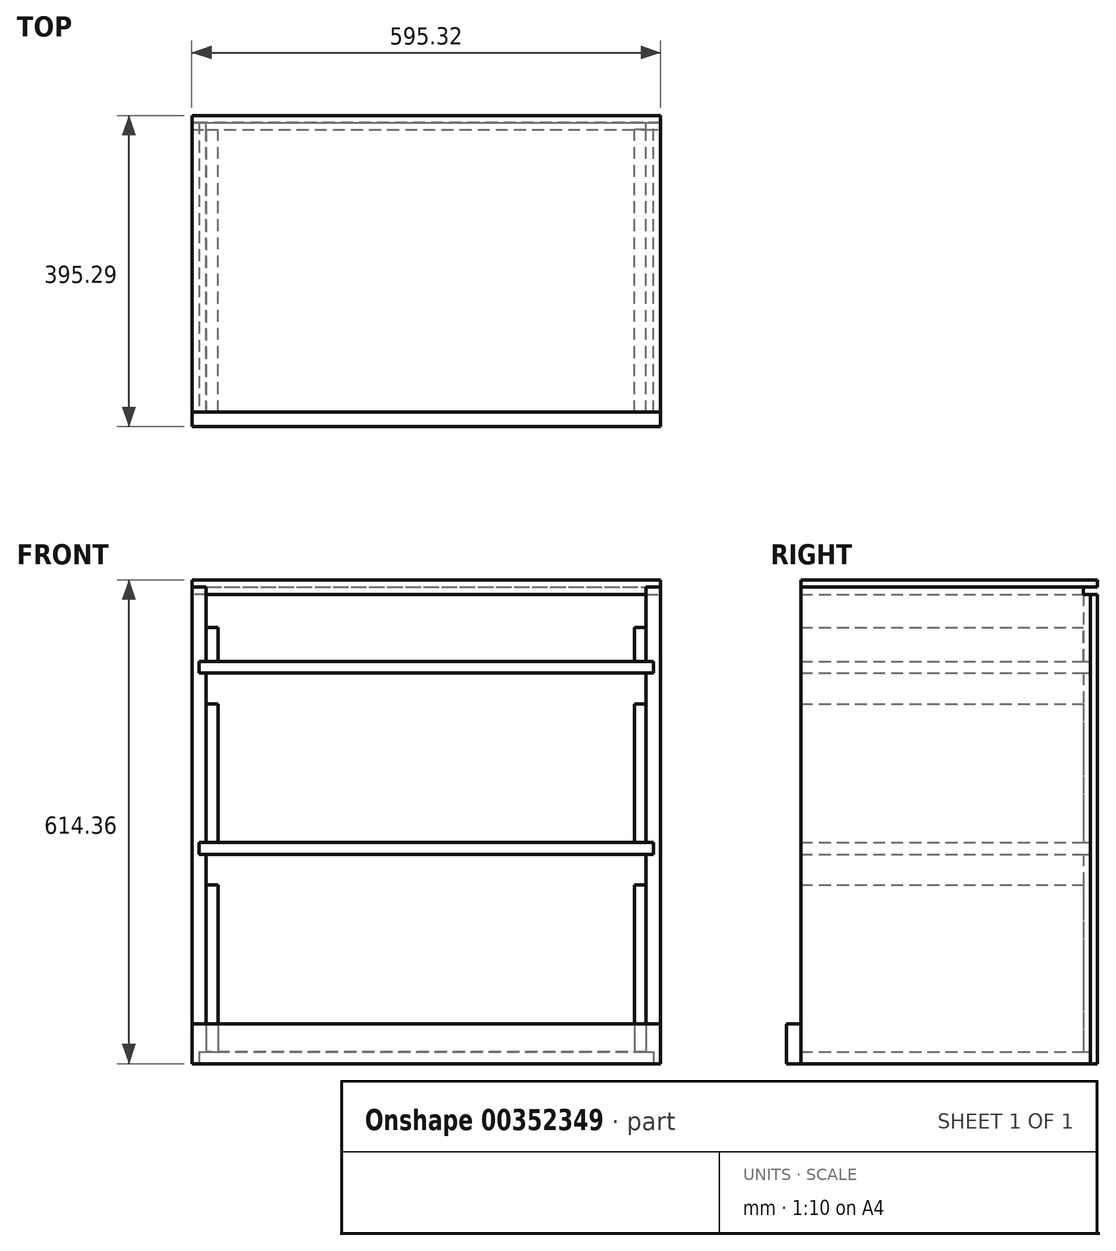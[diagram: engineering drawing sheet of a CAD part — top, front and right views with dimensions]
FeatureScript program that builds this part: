
annotation { "Feature Type Name" : "Feature", "Feature Type Description" : "" }
export const myFeature = defineFeature(function(context is Context, id is Id, definition is map)
    precondition{}
    {
        {
            var Q0;
            Q0=qCreatedBy(makeId("Top.planeOp"),FACE);
            var sketch = newSketch(context, id + "F0", { "sketchPlane" : qUnion([Q0])});
            skLineSegment(sketch, "E0.bottom", {"start": v(-266.7, 177.8) * mm, "end": v(266.7, 177.8) * mm, "construction": true});
            skLineSegment(sketch, "E0.top", {"start": v(-266.7, -177.8) * mm, "end": v(266.7, -177.8) * mm, "construction": true});
            skLineSegment(sketch, "E0.left", {"start": v(-266.7, 177.8) * mm, "end": v(-266.7, -177.8) * mm, "construction": true});
            skLineSegment(sketch, "E0.right", {"start": v(266.7, 177.8) * mm, "end": v(266.7, -177.8) * mm, "construction": true});
            skLineSegment(sketch, "E1", {"start": v(-297.66, 199.23) * mm, "end": v(-297.66, 190.1) * mm});
            skLineSegment(sketch, "E2", {"start": v(-297.66, 190.1) * mm, "end": v(-279.4, 190.1) * mm});
            skLineSegment(sketch, "E3", {"start": v(-279.4, 190.1) * mm, "end": v(-279.4, 180.97) * mm});
            skLineSegment(sketch, "E4.MirrorCS", {"start": v(279.4, 190.1) * mm, "end": v(279.4, 180.97) * mm});
            skLineSegment(sketch, "E5.MirrorCS", {"start": v(297.66, 199.23) * mm, "end": v(297.66, 190.1) * mm});
            skLineSegment(sketch, "E6.MirrorCS", {"start": v(297.66, 190.1) * mm, "end": v(279.4, 190.1) * mm});
            skLineSegment(sketch, "E7", {"start": v(-297.66, 199.23) * mm, "end": v(297.66, 199.23) * mm});
            skLineSegment(sketch, "E8", {"start": v(-279.4, 180.97) * mm, "end": v(279.4, 180.97) * mm});
            skLineSegment(sketch, "E9.bottom", {"start": v(-297.66, -196.06) * mm, "end": v(297.66, -196.06) * mm});
            skLineSegment(sketch, "E9.top", {"start": v(-297.66, -177.8) * mm, "end": v(297.66, -177.8) * mm});
            skLineSegment(sketch, "E9.left", {"start": v(-297.66, -196.06) * mm, "end": v(-297.66, -177.8) * mm});
            skLineSegment(sketch, "E9.right", {"start": v(297.66, -196.06) * mm, "end": v(297.66, -177.8) * mm});
            skSolve(sketch);
        }
        {
            var Q0;
            Q0=qCreatedBy(makeId("Top.planeOp"),FACE);
            var sketch = newSketch(context, id + "F1", { "sketchPlane" : qUnion([Q0])});
            skLineSegment(sketch, "E10.bottom", {"start": v(-297.66, 190.1) * mm, "end": v(-279.4, 190.1) * mm});
            skLineSegment(sketch, "E10.top", {"start": v(-297.66, -177.8) * mm, "end": v(-279.4, -177.8) * mm});
            skLineSegment(sketch, "E10.left", {"start": v(-297.66, 190.1) * mm, "end": v(-297.66, -177.8) * mm});
            skLineSegment(sketch, "E10.right", {"start": v(-279.4, 190.1) * mm, "end": v(-279.4, -177.8) * mm});
            skLineSegment(sketch, "E11.MirrorCS", {"start": v(297.66, -177.8) * mm, "end": v(279.4, -177.8) * mm});
            skLineSegment(sketch, "E12.MirrorCS", {"start": v(297.66, 190.1) * mm, "end": v(279.4, 190.1) * mm});
            skLineSegment(sketch, "E13.MirrorCS", {"start": v(297.66, 190.1) * mm, "end": v(297.66, -177.8) * mm});
            skLineSegment(sketch, "E14.MirrorCS", {"start": v(279.4, 190.1) * mm, "end": v(279.4, -177.8) * mm});
            skSolve(sketch);
        }
        {
            var Q0;
            Q0=qCreatedBy(makeId("Front.planeOp"),FACE);
            var sketch = newSketch(context, id + "F2", { "sketchPlane" : qUnion([Q0])});
            skLineSegment(sketch, "E15.bottom", {"start": v(-288.53, 15.08) * mm, "end": v(288.53, 15.08) * mm});
            skLineSegment(sketch, "E15.top", {"start": v(-288.53, 0) * mm, "end": v(288.53, 0) * mm});
            skLineSegment(sketch, "E15.left", {"start": v(-288.53, 15.08) * mm, "end": v(-288.53, 0) * mm});
            skLineSegment(sketch, "E15.right", {"start": v(288.53, 15.08) * mm, "end": v(288.53, 0) * mm});
            skLineSegment(sketch, "E16.bottom", {"start": v(-288.53, 280.99) * mm, "end": v(288.53, 280.99) * mm});
            skLineSegment(sketch, "E16.top", {"start": v(-288.53, 265.9) * mm, "end": v(288.53, 265.9) * mm});
            skLineSegment(sketch, "E16.left", {"start": v(-288.53, 280.99) * mm, "end": v(-288.53, 265.9) * mm});
            skLineSegment(sketch, "E16.right", {"start": v(288.53, 280.99) * mm, "end": v(288.53, 265.9) * mm});
            skLineSegment(sketch, "E17.bottom", {"start": v(-288.53, 511.18) * mm, "end": v(288.53, 511.18) * mm});
            skLineSegment(sketch, "E17.top", {"start": v(-288.53, 496.1) * mm, "end": v(288.53, 496.1) * mm});
            skLineSegment(sketch, "E17.left", {"start": v(-288.53, 511.18) * mm, "end": v(-288.53, 496.1) * mm});
            skLineSegment(sketch, "E17.right", {"start": v(288.53, 511.18) * mm, "end": v(288.53, 496.1) * mm});
            skLineSegment(sketch, "E18", {"start": v(-288.53, 605.23) * mm, "end": v(288.53, 605.23) * mm, "construction": true});
            skSolve(sketch);
        }
        {
            var Q0;
            Q0=qCreatedBy(makeId("Front.planeOp"),FACE);
            var sketch = newSketch(context, id + "F3", { "sketchPlane" : qUnion([Q0])});
            skLineSegment(sketch, "E19", {"start": v(-297.66, 614.36) * mm, "end": v(-297.66, 605.23) * mm});
            skLineSegment(sketch, "E20", {"start": v(-297.66, 605.23) * mm, "end": v(-279.4, 605.23) * mm});
            skLineSegment(sketch, "E21", {"start": v(-279.4, 605.23) * mm, "end": v(-279.4, 596.1) * mm});
            skLineSegment(sketch, "E22.MirrorCS", {"start": v(279.4, 605.23) * mm, "end": v(279.4, 596.1) * mm});
            skLineSegment(sketch, "E23.MirrorCS", {"start": v(297.66, 605.23) * mm, "end": v(279.4, 605.23) * mm});
            skLineSegment(sketch, "E24.MirrorCS", {"start": v(297.66, 614.36) * mm, "end": v(297.66, 605.23) * mm});
            skLineSegment(sketch, "E25", {"start": v(-297.66, 614.36) * mm, "end": v(297.66, 614.36) * mm});
            skLineSegment(sketch, "E26", {"start": v(-279.4, 596.1) * mm, "end": v(279.4, 596.1) * mm});
            skSolve(sketch);
        }
        {
            var Q0;
            Q0=qCreatedBy(makeId("Front.planeOp"),FACE);
            var sketch = newSketch(context, id + "F4", { "sketchPlane" : qUnion([Q0])});
            skLineSegment(sketch, "E27.bottom", {"start": v(-279.4, 227.01) * mm, "end": v(-264.32, 227.01) * mm});
            skLineSegment(sketch, "E27.top", {"start": v(-279.4, 15.08) * mm, "end": v(-264.32, 15.08) * mm});
            skLineSegment(sketch, "E27.left", {"start": v(-279.4, 227.01) * mm, "end": v(-279.4, 15.08) * mm});
            skLineSegment(sketch, "E27.right", {"start": v(-264.32, 227.01) * mm, "end": v(-264.32, 15.08) * mm});
            skLineSegment(sketch, "E28.bottom", {"start": v(-279.4, 457.2) * mm, "end": v(-264.32, 457.2) * mm});
            skLineSegment(sketch, "E28.top", {"start": v(-279.4, 280.99) * mm, "end": v(-264.32, 280.99) * mm});
            skLineSegment(sketch, "E28.left", {"start": v(-279.4, 457.2) * mm, "end": v(-279.4, 280.99) * mm});
            skLineSegment(sketch, "E28.right", {"start": v(-264.32, 457.2) * mm, "end": v(-264.32, 280.99) * mm});
            skLineSegment(sketch, "E29.bottom", {"start": v(-279.4, 511.18) * mm, "end": v(-264.32, 511.18) * mm});
            skLineSegment(sketch, "E29.top", {"start": v(-279.4, 554.04) * mm, "end": v(-264.32, 554.04) * mm});
            skLineSegment(sketch, "E29.left", {"start": v(-279.4, 511.18) * mm, "end": v(-279.4, 554.04) * mm});
            skLineSegment(sketch, "E29.right", {"start": v(-264.32, 511.18) * mm, "end": v(-264.32, 554.04) * mm});
            skLineSegment(sketch, "E30.MirrorCS", {"start": v(279.4, 280.99) * mm, "end": v(264.32, 280.99) * mm});
            skLineSegment(sketch, "E31.MirrorCS", {"start": v(279.4, 457.2) * mm, "end": v(264.32, 457.2) * mm});
            skLineSegment(sketch, "E32.MirrorCS", {"start": v(279.4, 15.08) * mm, "end": v(264.32, 15.08) * mm});
            skLineSegment(sketch, "E33.MirrorCS", {"start": v(279.4, 554.04) * mm, "end": v(264.32, 554.04) * mm});
            skLineSegment(sketch, "E34.MirrorCS", {"start": v(279.4, 511.18) * mm, "end": v(264.32, 511.18) * mm});
            skLineSegment(sketch, "E35.MirrorCS", {"start": v(279.4, 227.01) * mm, "end": v(264.32, 227.01) * mm});
            skLineSegment(sketch, "E36.MirrorCS", {"start": v(264.32, 227.01) * mm, "end": v(264.32, 15.08) * mm});
            skLineSegment(sketch, "E37.MirrorCS", {"start": v(279.4, 227.01) * mm, "end": v(279.4, 15.08) * mm});
            skLineSegment(sketch, "E38.MirrorCS", {"start": v(264.32, 511.18) * mm, "end": v(264.32, 554.04) * mm});
            skLineSegment(sketch, "E39.MirrorCS", {"start": v(279.4, 511.18) * mm, "end": v(279.4, 554.04) * mm});
            skLineSegment(sketch, "E40.MirrorCS", {"start": v(264.32, 457.2) * mm, "end": v(264.32, 280.99) * mm});
            skLineSegment(sketch, "E41.MirrorCS", {"start": v(279.4, 457.2) * mm, "end": v(279.4, 280.99) * mm});
            skLineSegment(sketch, "E42", {"start": v(-279.4, 457.2) * mm, "end": v(-279.4, 496.1) * mm, "construction": true});
            skLineSegment(sketch, "E43", {"start": v(-279.4, 227.01) * mm, "end": v(-279.4, 265.9) * mm, "construction": true});
            skSolve(sketch);
        }
        {
            var Q0;
            Q0=qCreatedBy(makeId("Right.planeOp"),FACE);
            var sketch = newSketch(context, id + "F5", { "sketchPlane" : qUnion([Q0])});
            skLineSegment(sketch, "E44.bottom", {"start": v(180.97, 596.1) * mm, "end": v(199.23, 596.1) * mm});
            skLineSegment(sketch, "E44.top", {"start": v(180.97, 605.23) * mm, "end": v(199.23, 605.23) * mm});
            skLineSegment(sketch, "E44.left", {"start": v(180.97, 596.1) * mm, "end": v(180.97, 605.23) * mm});
            skLineSegment(sketch, "E44.right", {"start": v(199.23, 596.1) * mm, "end": v(199.23, 605.23) * mm});
            skSolve(sketch);
        }
        {
            var Q0;
            Q0=makeQuery(id+"F1.imprint","IMPRINT",FACE,{"disambiguationData":[TD([[makeQuery(id+"F1.imprint","IMPRINT",EDGE,{"derivedFrom":sQuery(id+"F1.wireOp",EDGE,"E10.bottom")}),-1.0]])]});
            var Q1;
            Q1=makeQuery(id+"F1.imprint","IMPRINT",FACE,{"disambiguationData":[TD([[makeQuery(id+"F1.imprint","IMPRINT",EDGE,{"derivedFrom":sQuery(id+"F1.wireOp",EDGE,"E11.MirrorCS")}),-1.0]])]});
            var Q2;
            Q2=makeQuery(id+"F0.imprint","IMPRINT",FACE,{"disambiguationData":[TD([[makeQuery(id+"F0.imprint","IMPRINT",EDGE,{"derivedFrom":sQuery(id+"F0.wireOp",EDGE,"E1")}),1.0]])]});
            extrude(context, id + "F6", {"entities" : qUnion([Q0, Q1, Q2]), "depth" : 605.23 * mm});
        }
        {
            var Q0;
            Q0=makeQuery(id+"F0.imprint","IMPRINT",FACE,{"disambiguationData":[TD([[makeQuery(id+"F0.imprint","IMPRINT",EDGE,{"derivedFrom":sQuery(id+"F0.wireOp",EDGE,"E9.bottom")}),1.0]])]});
            extrude(context, id + "F7", {"entities" : qUnion([Q0]), "depth" : 50.8 * mm});
        }
        {
            var Q0;
            Q0 = qSketchRegion(id + "F2", true);
            extrude(context, id + "F8", {"entities" : qUnion([Q0]), "operationType" : NewBodyOperationType.REMOVE, "oppositeDirection" : true, "depth" : 190.1 * mm, "hasSecondDirection" : true, "secondDirectionOppositeDirection" : false, "secondDirectionDepth" : 177.8 * mm});
        }
        {
            var Q0;
            Q0 = qSketchRegion(id + "F2", true);
            var Q1;
            Q1=makeQuery(id+"F8.boolean.opBoolean","MERGE",FACE,{"derivedFrom":[makeQuery(id+"F6.opExtrude","SWEPT_FACE",FACE,{"disambiguationData":[OSD([sQuery(id+"F0.wireOp",EDGE,"E2")])]}),makeQuery(id+"F6.opExtrude","SWEPT_FACE",FACE,{"disambiguationData":[OSD([sQuery(id+"F0.wireOp",EDGE,"E6.MirrorCS")])]}),makeQuery(id+"F8.opExtrude","CAP_FACE",FACE,{"disambiguationData":[OSD([sQuery(id+"F2.wireOp",EDGE,"E15.bottom"),sQuery(id+"F2.wireOp",EDGE,"E15.top"),sQuery(id+"F2.wireOp",EDGE,"E15.left"),sQuery(id+"F2.wireOp",EDGE,"E15.right")])],"isStart":false}),makeQuery(id+"F8.opExtrude","CAP_FACE",FACE,{"disambiguationData":[OSD([sQuery(id+"F2.wireOp",EDGE,"E16.bottom"),sQuery(id+"F2.wireOp",EDGE,"E16.top"),sQuery(id+"F2.wireOp",EDGE,"E16.left"),sQuery(id+"F2.wireOp",EDGE,"E16.right")])],"isStart":false}),makeQuery(id+"F8.opExtrude","CAP_FACE",FACE,{"disambiguationData":[OSD([sQuery(id+"F2.wireOp",EDGE,"E17.bottom"),sQuery(id+"F2.wireOp",EDGE,"E17.top"),sQuery(id+"F2.wireOp",EDGE,"E17.left"),sQuery(id+"F2.wireOp",EDGE,"E17.right")])],"isStart":false})]});
            var Q2;
            Q2=makeQuery(id+"F7.opExtrude","SWEPT_FACE",FACE,{"disambiguationData":[OSD([sQuery(id+"F0.wireOp",EDGE,"E9.top")])]});
            extrude(context, id + "F9", {"entities" : qUnion([Q0]), "endBoundEntityFace" : qUnion([Q1]), "depth" : 177.8 * mm, "hasSecondDirection" : true, "secondDirectionOppositeDirection" : true, "secondDirectionBoundEntityFace" : qUnion([Q2]), "secondDirectionDepth" : 190.1 * mm});
        }
        {
            var Q0;
            Q0 = qSketchRegion(id + "F3", true);
            extrude(context, id + "F10", {"entities" : qUnion([Q0]), "depth" : 177.8 * mm, "hasSecondDirection" : true, "secondDirectionOppositeDirection" : true, "secondDirectionDepth" : 199.23 * mm});
        }
        {
            var Q0;
            Q0 = qSketchRegion(id + "F5", true);
            var Q1;
            Q1=makeQuery(id+"F10.opExtrude","SWEPT_FACE",FACE,{"disambiguationData":[OSD([sQuery(id+"F3.wireOp",EDGE,"E19")])]});
            var Q2;
            Q2=makeQuery(id+"F10.opExtrude","SWEPT_FACE",FACE,{"disambiguationData":[OSD([sQuery(id+"F3.wireOp",EDGE,"E24.MirrorCS")])]});
            extrude(context, id + "F11", {"entities" : qUnion([Q0]), "operationType" : NewBodyOperationType.REMOVE, "endBound" : BoundingType.UP_TO_SURFACE, "oppositeDirection" : true, "endBoundEntityFace" : qUnion([Q1]), "depth" : 127 * mm, "hasSecondDirection" : true, "secondDirectionBound" : SecondDirectionBoundingType.UP_TO_SURFACE, "secondDirectionOppositeDirection" : false, "secondDirectionBoundEntityFace" : qUnion([Q2]), "secondDirectionDepth" : 127 * mm});
        }
        {
            var Q0;
            Q0 = qSketchRegion(id + "F4", true);
            extrude(context, id + "F12", {"entities" : qUnion([Q0]), "depth" : 177.8 * mm, "hasSecondDirection" : true, "secondDirectionOppositeDirection" : true, "secondDirectionDepth" : 180.97 * mm});
        }
    });
